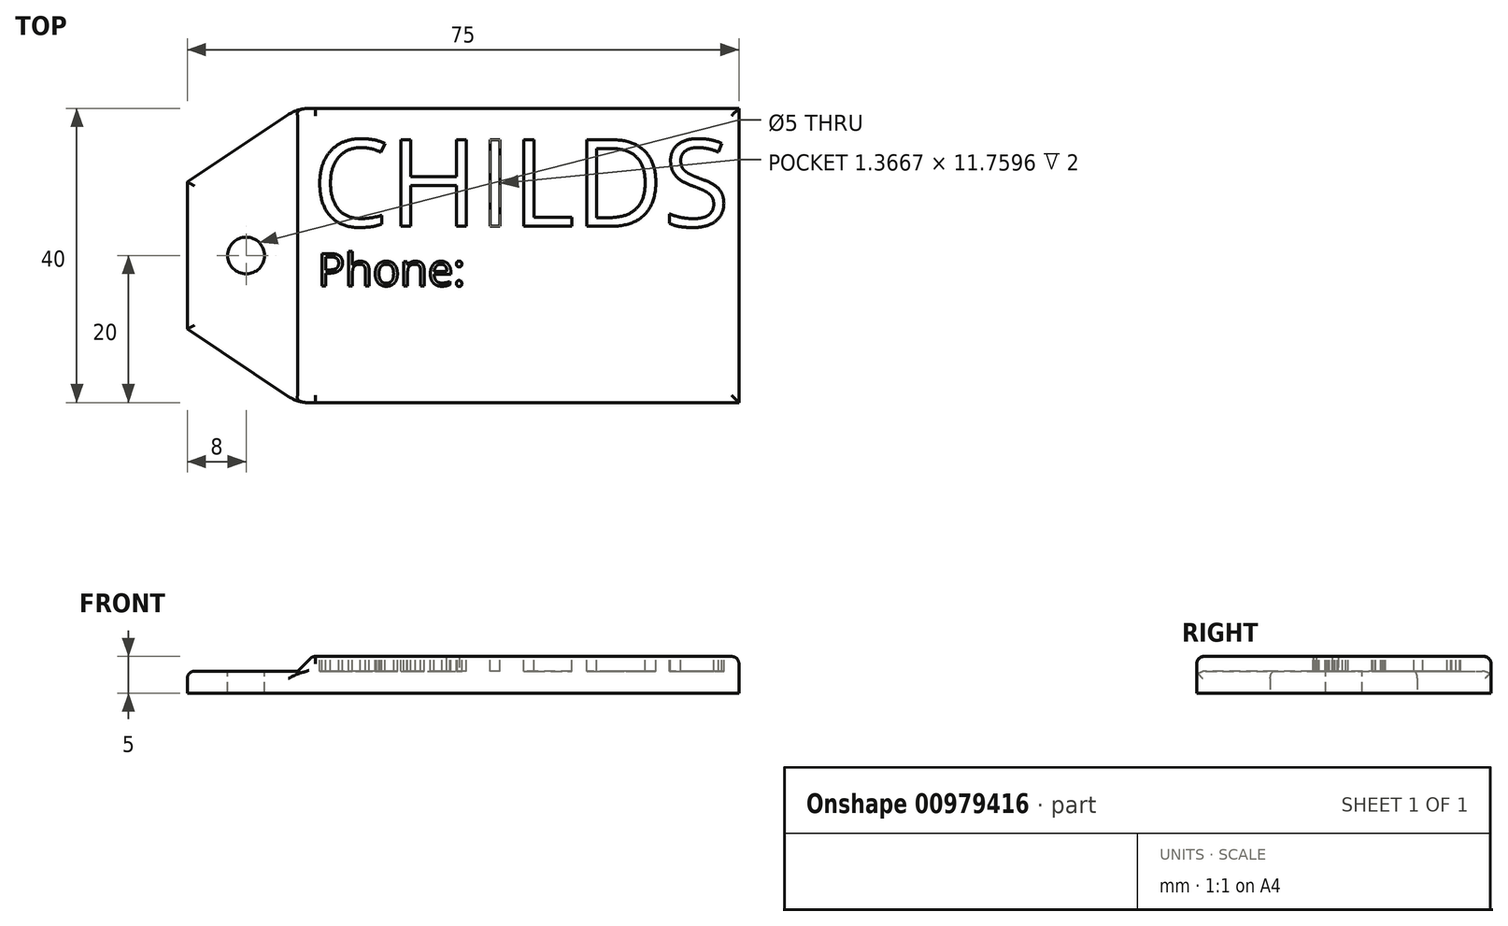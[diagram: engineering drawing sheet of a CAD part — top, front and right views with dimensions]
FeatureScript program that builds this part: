
annotation { "Feature Type Name" : "Feature", "Feature Type Description" : "" }
export const myFeature = defineFeature(function(context is Context, id is Id, definition is map)
    precondition{}
    {
        {
            var Q0;
            Q0=qCreatedBy(makeId("Top.planeOp"),FACE);
            var sketch = newSketch(context, id + "F0", { "sketchPlane" : qUnion([Q0])});
            skLineSegment(sketch, "E0.bottom", {"start": v(30, -20) * mm, "end": v(-30, -20) * mm});
            skLineSegment(sketch, "E0.top", {"start": v(30, 20) * mm, "end": v(-30, 20) * mm});
            skLineSegment(sketch, "E0.left", {"start": v(30, -20) * mm, "end": v(30, 20) * mm});
            skLineSegment(sketch, "E0.right", {"start": v(-30, -20) * mm, "end": v(-30, 20) * mm});
            skPoint(sketch, "E0.middle", {"position": v(0, 0) * mm});
            skLineSegment(sketch, "E1", {"start": v(-45, 10) * mm, "end": v(-45, 0) * mm});
            skLineSegment(sketch, "E2", {"start": v(-45, -10) * mm, "end": v(-45, 0) * mm});
            skPoint(sketch, "E2.startSnap0", {"position": v(-45, 10) * mm});
            skPoint(sketch, "E3.orphan", {"position": v(-45, 20) * mm});
            skLineSegment(sketch, "E4", {"start": v(-45, 10) * mm, "end": v(-30, 20) * mm});
            skLineSegment(sketch, "E5", {"start": v(-45, -10) * mm, "end": v(-30, -20) * mm});
            skPoint(sketch, "E6.start.orphan", {"position": v(-30, 0) * mm});
            skSolve(sketch);
        }
        {
            var Q0;
            Q0=makeQuery(id+"F0.imprint","IMPRINT",FACE,{"disambiguationData":[TD([[makeQuery(id+"F0.imprint","IMPRINT",EDGE,{"derivedFrom":sQuery(id+"F0.wireOp",EDGE,"E0.bottom")}),-1.0]])]});
            extrude(context, id + "F1", {"entities" : qUnion([Q0]), "depth" : 5 * mm, "offsetDistance" : 25 * mm});
        }
        {
            var Q0;
            Q0=makeQuery(id+"F0.imprint","IMPRINT",FACE,{"disambiguationData":[TD([[makeQuery(id+"F0.imprint","IMPRINT",EDGE,{"derivedFrom":sQuery(id+"F0.wireOp",EDGE,"E0.right")}),1.0]])]});
            extrude(context, id + "F2", {"entities" : qUnion([Q0]), "operationType" : NewBodyOperationType.ADD, "depth" : 3 * mm, "offsetDistance" : 25 * mm});
        }
        {
            var Q0;
            Q0=makeQuery(id+"F1.opExtrude","CAP_EDGE",EDGE,{"disambiguationData":[OSD([sQuery(id+"F0.wireOp",EDGE,"E0.right")])],"isStart":false});
            chamfer(context, id + "F3", {"entities" : qUnion([Q0]), "width" : 2 * mm, "tangentPropagation" : true});
        }
        {
            var Q0;
            Q0=makeQuery(id+"F1.opExtrude","CAP_EDGE",EDGE,{"disambiguationData":[OSD([sQuery(id+"F0.wireOp",EDGE,"E0.bottom")])],"isStart":false});
            var Q1;
            Q1=makeQuery(id+"F1.opExtrude","CAP_EDGE",EDGE,{"disambiguationData":[OSD([sQuery(id+"F0.wireOp",EDGE,"E0.top")])],"isStart":false});
            var Q2;
            Q2=makeQuery(id+"F1.opExtrude","CAP_EDGE",EDGE,{"disambiguationData":[OSD([sQuery(id+"F0.wireOp",EDGE,"E0.left")])],"isStart":false});
            fillet(context, id + "F4", {"entities" : qUnion([Q0, Q1, Q2]), "radius" : 1 * mm, "tangentPropagation" : true, "allowEdgeOverflow" : false});
        }
        {
            var Q0;
            {var subQ0=sQuery(id+"F0.wireOp",EDGE,"E0.right");Q0=makeQuery(id+"F3.opChamfer","BLEND_EDGE",EDGE,{"blendedFrom":[makeQuery(id+"F1.opExtrude","CAP_EDGE",EDGE,{"disambiguationData":[OSD([subQ0])],"isStart":false}),makeQuery(id+"F1.opExtrude","CAP_FACE",FACE,{"disambiguationData":[OSD([sQuery(id+"F0.wireOp",EDGE,"E0.bottom"),sQuery(id+"F0.wireOp",EDGE,"E0.top"),sQuery(id+"F0.wireOp",EDGE,"E0.left"),subQ0])],"isStart":false})],"blendedInto":[makeQuery(id+"F1.opExtrude","CAP_FACE",FACE,{"disambiguationData":[OSD([sQuery(id+"F0.wireOp",EDGE,"E0.bottom"),sQuery(id+"F0.wireOp",EDGE,"E0.top"),sQuery(id+"F0.wireOp",EDGE,"E0.left"),subQ0])],"isStart":false})]});}
            fillet(context, id + "F5", {"entities" : qUnion([Q0]), "radius" : 1 * mm, "tangentPropagation" : true, "allowEdgeOverflow" : false});
        }
        {
            var Q0;
            Q0=makeQuery(id+"F2.opExtrude","CAP_EDGE",EDGE,{"disambiguationData":[OSD([sQuery(id+"F0.wireOp",EDGE,"E1"),sQuery(id+"F0.wireOp",EDGE,"E2")])],"isStart":false});
            var Q1;
            Q1=makeQuery(id+"F2.opExtrude","CAP_EDGE",EDGE,{"disambiguationData":[OSD([sQuery(id+"F0.wireOp",EDGE,"E5")])],"isStart":false});
            var Q2;
            Q2=makeQuery(id+"F2.opExtrude","CAP_EDGE",EDGE,{"disambiguationData":[OSD([sQuery(id+"F0.wireOp",EDGE,"E4")])],"isStart":false});
            fillet(context, id + "F6", {"entities" : qUnion([Q0, Q1, Q2]), "radius" : 1 * mm, "tangentPropagation" : true, "allowEdgeOverflow" : false});
        }
        {
            var Q0;
            {var subQ0=sQuery(id+"F0.wireOp",EDGE,"E5");var subQ1=sQuery(id+"F0.wireOp",EDGE,"E0.right");var subQ2=sQuery(id+"F0.wireOp",EDGE,"E0.bottom");Q0=makeQuery(id+"F2.boolean.opBoolean","MERGE",EDGE,{"derivedFrom":[makeQuery(id+"F1.opExtrude","SWEPT_EDGE",EDGE,{"disambiguationData":[OSD([subQ2,subQ1,subQ0])]}),makeQuery(id+"F2.opExtrude","SWEPT_EDGE",EDGE,{"disambiguationData":[OSD([subQ2,subQ1,subQ0])]})]});}
            fillet(context, id + "F7", {"entities" : qUnion([Q0]), "radius" : 5 * mm, "tangentPropagation" : true, "allowEdgeOverflow" : false});
        }
        {
            var Q0;
            {var subQ0=sQuery(id+"F0.wireOp",EDGE,"E4");var subQ1=sQuery(id+"F0.wireOp",EDGE,"E0.right");var subQ2=sQuery(id+"F0.wireOp",EDGE,"E0.top");Q0=makeQuery(id+"F2.boolean.opBoolean","MERGE",EDGE,{"derivedFrom":[makeQuery(id+"F1.opExtrude","SWEPT_EDGE",EDGE,{"disambiguationData":[OSD([subQ2,subQ1,subQ0])]}),makeQuery(id+"F2.opExtrude","SWEPT_EDGE",EDGE,{"disambiguationData":[OSD([subQ2,subQ1,subQ0])]})]});}
            fillet(context, id + "F8", {"entities" : qUnion([Q0]), "radius" : 5 * mm, "tangentPropagation" : true, "allowEdgeOverflow" : false});
        }
        {
            var Q0;
            Q0=makeQuery(id+"F2.opExtrude","CAP_FACE",FACE,{"disambiguationData":[OSD([sQuery(id+"F0.wireOp",EDGE,"E0.right"),sQuery(id+"F0.wireOp",EDGE,"E1"),sQuery(id+"F0.wireOp",EDGE,"E2"),sQuery(id+"F0.wireOp",EDGE,"E4"),sQuery(id+"F0.wireOp",EDGE,"E5")])],"isStart":false});
            var sketch = newSketch(context, id + "F9", { "sketchPlane" : qUnion([Q0])});
            skPoint(sketch, "E7", {"position": v(-35.24, 0) * mm});
            skPoint(sketch, "E8.orphan", {"position": v(-30, 0) * mm});
            skPoint(sketch, "E9", {"position": v(-37, 0) * mm});
            skCircle(sketch, "E10", {"center": v(-37, 0) * mm, "radius": 2.5 * mm});
            skSolve(sketch);
        }
        {
            var Q0;
            Q0 = qSketchRegion(id + "F9", true);
            extrude(context, id + "F10", {"entities" : qUnion([Q0]), "operationType" : NewBodyOperationType.REMOVE, "oppositeDirection" : true, "depth" : 25 * mm, "offsetDistance" : 25 * mm});
        }
        {
            var Q0;
            Q0=makeQuery(id+"F1.opExtrude","CAP_FACE",FACE,{"disambiguationData":[OSD([sQuery(id+"F0.wireOp",EDGE,"E0.bottom"),sQuery(id+"F0.wireOp",EDGE,"E0.top"),sQuery(id+"F0.wireOp",EDGE,"E0.left"),sQuery(id+"F0.wireOp",EDGE,"E0.right")])],"isStart":false});
            var sketch = newSketch(context, id + "F11", { "sketchPlane" : qUnion([Q0])});
            skText(sketch, "E11", { "text": "CHILDS", "fontName": "OpenSans-Regular.ttf"});
            skText(sketch, "E12", { "text": "Phone:", "fontName": "OpenSans-Regular.ttf"});
            const initialGuessF11  = {"E11": [-0.028, 0.00397, 1, 0, 0.01186], "E12": [-0.02728, -0.00412, 1, 0, 0.00443]};
            skSetInitialGuess(sketch, initialGuessF11);
            skSolve(sketch);
        }
        {
            var Q0;
            Q0 = qSketchRegion(id + "F11", true);
            extrude(context, id + "F12", {"entities" : qUnion([Q0]), "operationType" : NewBodyOperationType.REMOVE, "oppositeDirection" : true, "depth" : 2 * mm, "offsetDistance" : 25 * mm});
        }
    });
